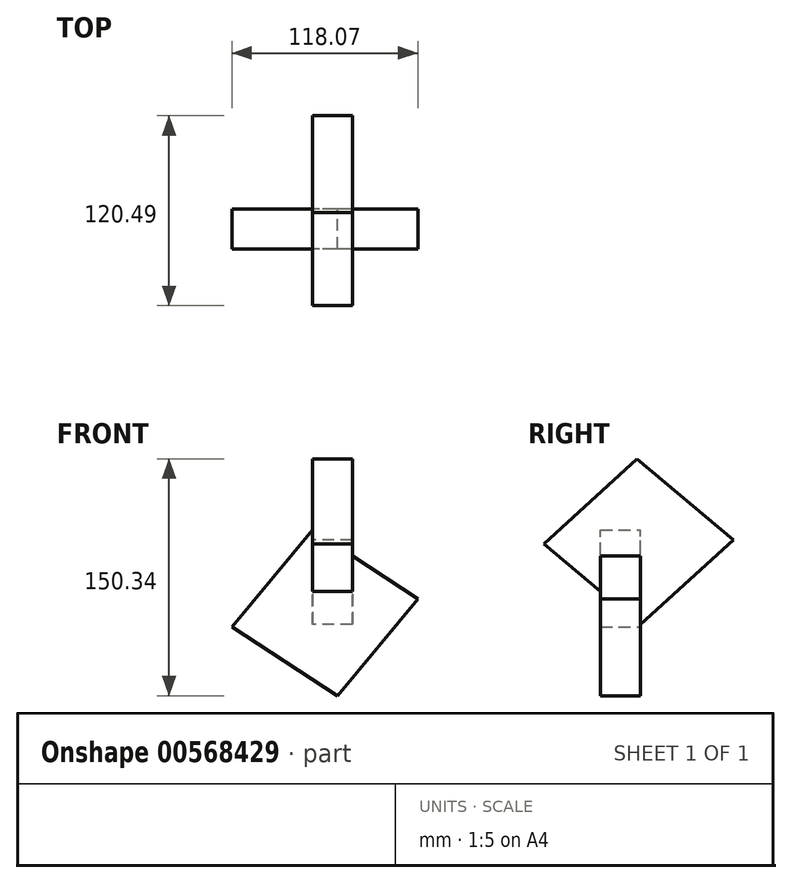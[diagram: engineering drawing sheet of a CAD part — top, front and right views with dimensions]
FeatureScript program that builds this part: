
annotation { "Feature Type Name" : "Feature", "Feature Type Description" : "" }
export const myFeature = defineFeature(function(context is Context, id is Id, definition is map)
    precondition{}
    {
        {
            var Q0;
            Q0=qCreatedBy(makeId("Front.planeOp"),FACE);
            var sketch = newSketch(context, id + "F0", { "sketchPlane" : qUnion([Q0])});
            skLineSegment(sketch, "E0", {"start": v(0, 90.52) * mm, "end": v(66.99, 46.78) * mm});
            skLineSegment(sketch, "E1", {"start": v(66.99, 46.78) * mm, "end": v(15.91, -14.8) * mm});
            skLineSegment(sketch, "E2", {"start": v(15.91, -14.8) * mm, "end": v(-51.08, 28.94) * mm});
            skLineSegment(sketch, "E3", {"start": v(-51.08, 28.94) * mm, "end": v(0, 90.52) * mm});
            skSolve(sketch);
        }
        {
            var Q0;
            Q0 = qSketchRegion(id + "F0", true);
            extrude(context, id + "F1", {"entities" : qUnion([Q0]), "depth" : 25.4 * mm, "offsetDistance" : 25.4 * mm});
        }
        {
            var Q0;
            Q0=qCreatedBy(makeId("Right.planeOp"),FACE);
            var sketch = newSketch(context, id + "F2", { "sketchPlane" : qUnion([Q0])});
            skLineSegment(sketch, "E4", {"start": v(-61.41, 81.61) * mm, "end": v(-2.33, 135.55) * mm});
            skLineSegment(sketch, "E5", {"start": v(-2.33, 135.55) * mm, "end": v(59.08, 84.28) * mm});
            skLineSegment(sketch, "E6", {"start": v(59.08, 84.28) * mm, "end": v(0, 30.34) * mm});
            skLineSegment(sketch, "E7", {"start": v(-61.41, 81.61) * mm, "end": v(0, 30.34) * mm});
            skSolve(sketch);
        }
        {
            var Q0;
            Q0 = qSketchRegion(id + "F2", true);
            extrude(context, id + "F3", {"entities" : qUnion([Q0]), "operationType" : NewBodyOperationType.ADD, "depth" : 25.4 * mm, "offsetDistance" : 25.4 * mm});
        }
    });
